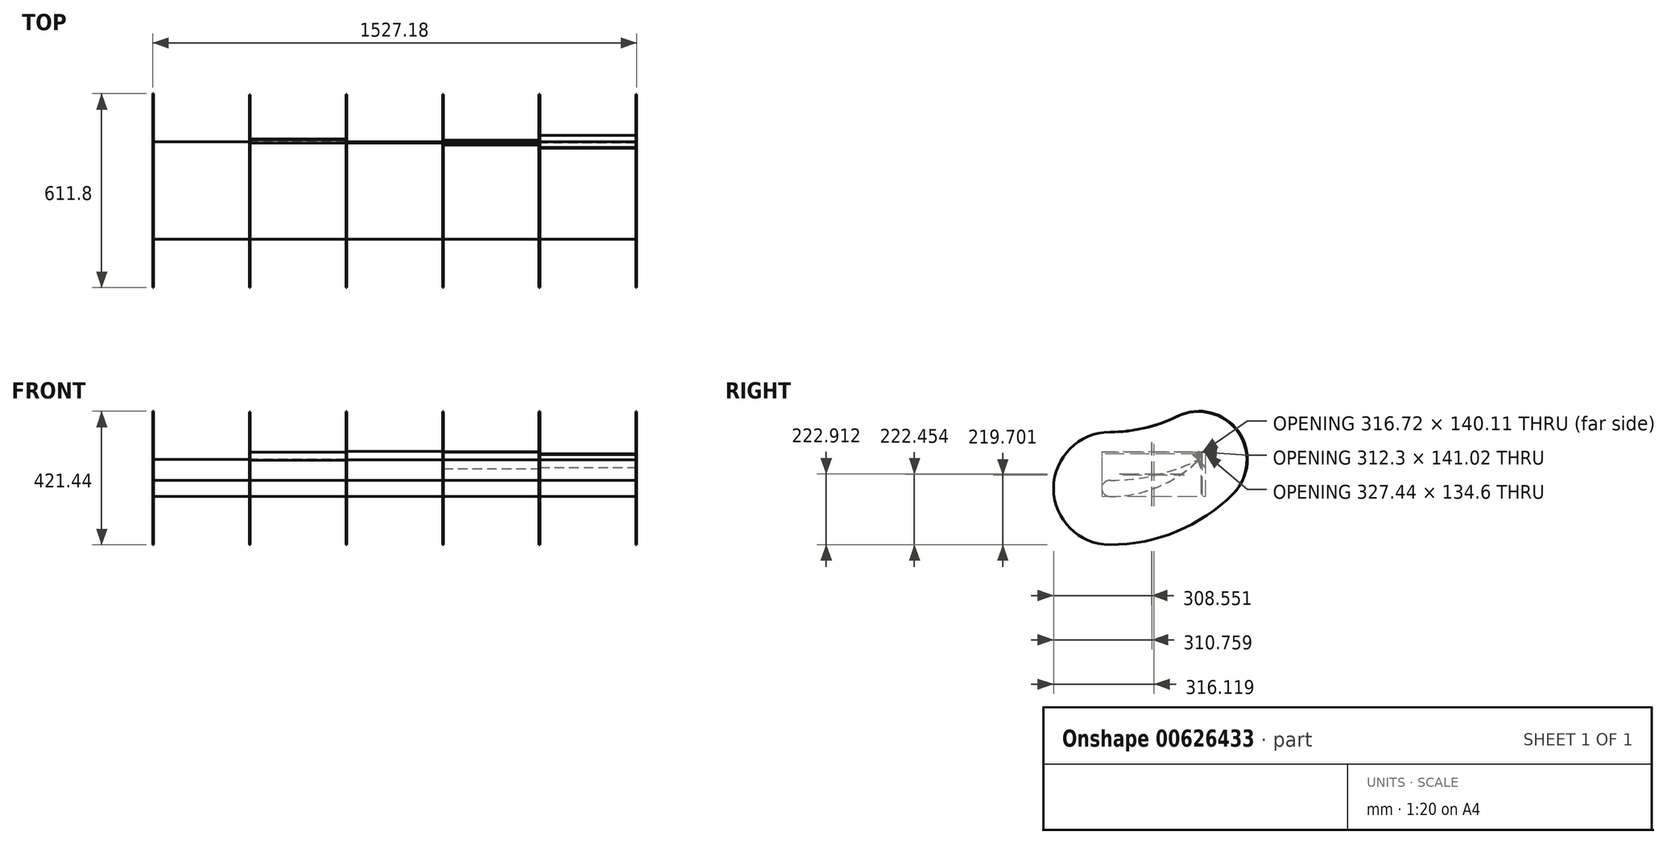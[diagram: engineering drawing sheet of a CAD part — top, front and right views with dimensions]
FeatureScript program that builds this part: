
annotation { "Feature Type Name" : "Feature", "Feature Type Description" : "" }
export const myFeature = defineFeature(function(context is Context, id is Id, definition is map)
    precondition{}
    {
        {
            var Q0;
            Q0=qCreatedBy(makeId("Right.planeOp"),FACE);
            var sketch = newSketch(context, id + "F0", { "sketchPlane" : qUnion([Q0])});
            skArc(sketch, "E0", {"start": v(0, -398.24) * mm, "mid": v(152.4, -367.93) * mm, "end": v(281.6, -281.6) * mm});
            skArc(sketch, "E1", {"start": v(0, -398.24) * mm, "mid": v(-25.4, -372.84) * mm, "end": v(0, -347.44) * mm});
            skArc(sketch, "E2", {"start": v(0, -347.44) * mm, "mid": v(144.6, -330.76) * mm, "end": v(281.6, -281.6) * mm});
            skLineSegment(sketch, "E3", {"start": v(0, 0) * mm, "end": v(281.6, -281.6) * mm});
            skSolve(sketch);
        }
        {
            var Q0;
            Q0=qSketchRegion(id+"F0",true);
            extrude(context, id + "F1", {"entities" : qUnion([Q0]), "depth" : 1524 * mm, "offsetDistance" : 25.4 * mm});
        }
        {
            var Q0;
            Q0=makeQuery(id+"F1.opExtrude","CAP_VERTEX",VERTEX,{"disambiguationData":[OSD([sQuery(id+"F0.wireOp",EDGE,"E0"),sQuery(id+"F0.wireOp",EDGE,"E1"),sQuery(id+"F0.wireOp",EDGE,"b3eccc3d-6429-4b34-9fe6-7e9520ef1e49")])],"isStart":false});
            var Q1;
            Q1=makeQuery(id+"F1.opExtrude","CAP_VERTEX",VERTEX,{"disambiguationData":[OSD([sQuery(id+"F0.wireOp",EDGE,"E1"),sQuery(id+"F0.wireOp",EDGE,"E2"),sQuery(id+"F0.wireOp",EDGE,"b3eccc3d-6429-4b34-9fe6-7e9520ef1e49")])],"isStart":false});
            var Q2;
            Q2=makeQuery(id+"F1.opExtrude","CAP_VERTEX",VERTEX,{"disambiguationData":[OSD([sQuery(id+"F0.wireOp",EDGE,"E0"),sQuery(id+"F0.wireOp",EDGE,"E2")])],"isStart":false});
            cPlane(context, id + "F2", {"entities" : qUnion([Q0, Q1, Q2]), "cplaneType" : CPlaneType.THREE_POINT, "offset" : 25.4 * mm, "width" : 152.4 * mm, "height" : 152.4 * mm});
        }
        {
            var Q0;
            Q0=qCreatedBy(id+"F2.planeOp",FACE);
            var sketch = newSketch(context, id + "F3", { "sketchPlane" : qUnion([Q0])});
            skLineSegment(sketch, "E4", {"start": v(281.6, -281.6) * mm, "end": v(263.64, -263.64) * mm});
            skLineSegment(sketch, "E5", {"start": v(263.64, -263.64) * mm, "end": v(261.4, -265.88) * mm});
            skLineSegment(sketch, "E6", {"start": v(261.4, -265.88) * mm, "end": v(302.04, -306.53) * mm});
            skLineSegment(sketch, "E7", {"start": v(281.6, -281.6) * mm, "end": v(302.04, -306.53) * mm});
            skSolve(sketch);
        }
        {
            var Q0;
            Q0=makeQuery(id+"F3.imprint","IMPRINT",FACE,{"disambiguationData":[TD([[makeQuery(id+"F3.imprint","IMPRINT",EDGE,{"derivedFrom":sQuery(id+"F3.wireOp",EDGE,"E4")}),1.0]])]});
            extrude(context, id + "F4", {"entities" : qUnion([Q0]), "operationType" : NewBodyOperationType.ADD, "oppositeDirection" : true, "depth" : 304.8 * mm, "offsetDistance" : 25.4 * mm});
        }
        {
            var Q0;
            Q0=qCreatedBy(id+"F2.planeOp",FACE);
            cPlane(context, id + "F5", {"entities" : qUnion([Q0]), "cplaneType" : CPlaneType.OFFSET, "offset" : 304.8 * mm, "oppositeDirection" : true, "width" : 152.4 * mm, "height" : 152.4 * mm});
        }
        {
            var Q0;
            Q0=qCreatedBy(id+"F5.planeOp",FACE);
            var sketch = newSketch(context, id + "F6", { "sketchPlane" : qUnion([Q0])});
            skPoint(sketch, "E8.0", {"position": v(281.6, -281.6) * mm});
            skLineSegment(sketch, "E9", {"start": v(281.6, -281.6) * mm, "end": v(274.48, -257.22) * mm});
            skLineSegment(sketch, "E10", {"start": v(274.48, -257.22) * mm, "end": v(271.43, -258.1) * mm});
            skLineSegment(sketch, "E11", {"start": v(271.43, -258.1) * mm, "end": v(286.9, -311.1) * mm});
            skLineSegment(sketch, "E12", {"start": v(286.9, -311.1) * mm, "end": v(281.6, -281.6) * mm});
            skSolve(sketch);
        }
        {
            var Q0;
            Q0=qSketchRegion(id+"F6",true);
            extrude(context, id + "F7", {"entities" : qUnion([Q0]), "operationType" : NewBodyOperationType.ADD, "oppositeDirection" : true, "depth" : 304.8 * mm, "offsetDistance" : 25.4 * mm});
        }
        {
            var Q0;
            Q0=qCreatedBy(id+"F5.planeOp",FACE);
            cPlane(context, id + "F8", {"entities" : qUnion([Q0]), "cplaneType" : CPlaneType.OFFSET, "offset" : 304.8 * mm, "oppositeDirection" : true, "width" : 152.4 * mm, "height" : 152.4 * mm});
        }
        {
            var Q0;
            Q0=qCreatedBy(id+"F8.planeOp",FACE);
            var sketch = newSketch(context, id + "F9", { "sketchPlane" : qUnion([Q0])});
            skPoint(sketch, "E13.0", {"position": v(281.6, -281.6) * mm});
            skLineSegment(sketch, "E14", {"start": v(281.6, -281.6) * mm, "end": v(281.6, -256.2) * mm});
            skLineSegment(sketch, "E15", {"start": v(281.6, -256.2) * mm, "end": v(278.42, -256.2) * mm});
            skLineSegment(sketch, "E16", {"start": v(278.42, -256.2) * mm, "end": v(278.42, -284.14) * mm});
            skLineSegment(sketch, "E17", {"start": v(278.42, -284.14) * mm, "end": v(281.6, -281.6) * mm});
            skSolve(sketch);
        }
        {
            var Q0;
            Q0=qSketchRegion(id+"F9",true);
            extrude(context, id + "F10", {"entities" : qUnion([Q0]), "operationType" : NewBodyOperationType.ADD, "oppositeDirection" : true, "depth" : 304.8 * mm, "offsetDistance" : 25.4 * mm});
        }
        {
            var Q0;
            Q0=qCreatedBy(id+"F8.planeOp",FACE);
            cPlane(context, id + "F11", {"entities" : qUnion([Q0]), "cplaneType" : CPlaneType.OFFSET, "offset" : 304.8 * mm, "oppositeDirection" : true, "width" : 152.4 * mm, "height" : 152.4 * mm});
        }
        {
            var Q0;
            Q0=qCreatedBy(id+"F11.planeOp",FACE);
            cPlane(context, id + "F12", {"entities" : qUnion([Q0]), "cplaneType" : CPlaneType.OFFSET, "offset" : 304.8 * mm, "oppositeDirection" : true, "width" : 152.4 * mm, "height" : 152.4 * mm});
        }
        {
            var Q0;
            Q0=makeQuery(id+"F1.opExtrude","CAP_FACE",FACE,{"disambiguationData":[OSD([sQuery(id+"F0.wireOp",EDGE,"E0"),sQuery(id+"F0.wireOp",EDGE,"E1"),sQuery(id+"F0.wireOp",EDGE,"E2")])],"isStart":true});
            var sketch = newSketch(context, id + "F13", { "sketchPlane" : qUnion([Q0])});
            skArc(sketch, "E18.0", {"start": v(0, -195.04) * mm, "mid": v(-109.9, -182.36) * mm, "end": v(-214.03, -145) * mm});
            skArc(sketch, "E19.0", {"start": v(0, -550.64) * mm, "mid": v(177.8, -372.84) * mm, "end": v(0, -195.04) * mm});
            skArc(sketch, "E20.0", {"start": v(0, -550.64) * mm, "mid": v(-210.72, -508.73) * mm, "end": v(-389.36, -389.36) * mm});
            skArc(sketch, "E21", {"start": v(-214.03, -145) * mm, "mid": v(-405.42, -192.75) * mm, "end": v(-389.36, -389.36) * mm});
            skSolve(sketch);
        }
        {
            var Q0;
            Q0=qSketchRegion(id+"F13",true);
            extrude(context, id + "F14", {"entities" : qUnion([Q0]), "operationType" : NewBodyOperationType.ADD, "endBound" : BoundingType.SYMMETRIC, "depth" : 3.17 * mm, "offsetDistance" : 25.4 * mm});
        }
        {
            var Q0;
            Q0=qCreatedBy(id+"F11.planeOp",FACE);
            var sketch = newSketch(context, id + "F15", { "sketchPlane" : qUnion([Q0])});
            skArc(sketch, "E22.0", {"start": v(0, -195.04) * mm, "mid": v(108.76, -182.63) * mm, "end": v(211.93, -146.03) * mm});
            skArc(sketch, "E23.0", {"start": v(0, -550.64) * mm, "mid": v(210.72, -508.73) * mm, "end": v(389.36, -389.36) * mm});
            skArc(sketch, "E24", {"start": v(0, -195.04) * mm, "mid": v(-177.8, -372.84) * mm, "end": v(0, -550.64) * mm});
            skArc(sketch, "E25", {"start": v(211.93, -146.03) * mm, "mid": v(402.63, -193.33) * mm, "end": v(389.36, -389.36) * mm});
            skSolve(sketch);
        }
        {
            var Q0;
            Q0=qSketchRegion(id+"F15",true);
            extrude(context, id + "F16", {"entities" : qUnion([Q0]), "operationType" : NewBodyOperationType.ADD, "endBound" : BoundingType.SYMMETRIC, "depth" : 3.17 * mm, "offsetDistance" : 25.4 * mm});
        }
        {
            var Q0;
            Q0=qCreatedBy(id+"F8.planeOp",FACE);
            var sketch = newSketch(context, id + "F17", { "sketchPlane" : qUnion([Q0])});
            skArc(sketch, "E26.0", {"start": v(0, -195.04) * mm, "mid": v(108.76, -182.63) * mm, "end": v(211.93, -146.03) * mm});
            skArc(sketch, "E27.0", {"start": v(0, -550.64) * mm, "mid": v(210.72, -508.73) * mm, "end": v(389.36, -389.36) * mm});
            skArc(sketch, "E28", {"start": v(0, -195.04) * mm, "mid": v(-177.8, -372.84) * mm, "end": v(0, -550.64) * mm});
            skArc(sketch, "E29", {"start": v(211.93, -146.03) * mm, "mid": v(402.63, -193.33) * mm, "end": v(389.36, -389.36) * mm});
            skSolve(sketch);
        }
        {
            var Q0;
            Q0=qSketchRegion(id+"F17",true);
            extrude(context, id + "F18", {"entities" : qUnion([Q0]), "operationType" : NewBodyOperationType.ADD, "endBound" : BoundingType.SYMMETRIC, "depth" : 3.17 * mm, "offsetDistance" : 25.4 * mm});
        }
        {
            var Q0;
            Q0=qCreatedBy(id+"F5.planeOp",FACE);
            var sketch = newSketch(context, id + "F19", { "sketchPlane" : qUnion([Q0])});
            skArc(sketch, "E30.0", {"start": v(0, -195.04) * mm, "mid": v(108.76, -182.63) * mm, "end": v(211.93, -146.03) * mm});
            skArc(sketch, "E31.0", {"start": v(0, -550.64) * mm, "mid": v(210.72, -508.73) * mm, "end": v(389.36, -389.36) * mm});
            skArc(sketch, "E32", {"start": v(0, -195.04) * mm, "mid": v(-177.8, -372.84) * mm, "end": v(0, -550.64) * mm});
            skArc(sketch, "E33", {"start": v(211.93, -146.03) * mm, "mid": v(402.63, -193.33) * mm, "end": v(389.36, -389.36) * mm});
            skSolve(sketch);
        }
        {
            var Q0;
            Q0=qSketchRegion(id+"F19",true);
            extrude(context, id + "F20", {"entities" : qUnion([Q0]), "operationType" : NewBodyOperationType.ADD, "endBound" : BoundingType.SYMMETRIC, "depth" : 3.17 * mm, "offsetDistance" : 25.4 * mm});
        }
        {
            var Q0;
            Q0=qCreatedBy(id+"F2.planeOp",FACE);
            var sketch = newSketch(context, id + "F21", { "sketchPlane" : qUnion([Q0])});
            skArc(sketch, "E34.0", {"start": v(0, -195.04) * mm, "mid": v(108.76, -182.63) * mm, "end": v(211.93, -146.03) * mm});
            skArc(sketch, "E35.0", {"start": v(0, -550.64) * mm, "mid": v(210.72, -508.73) * mm, "end": v(389.36, -389.36) * mm});
            skArc(sketch, "E36", {"start": v(0, -195.04) * mm, "mid": v(-177.8, -372.84) * mm, "end": v(0, -550.64) * mm});
            skArc(sketch, "E37", {"start": v(211.93, -146.03) * mm, "mid": v(402.63, -193.33) * mm, "end": v(389.36, -389.36) * mm});
            skSolve(sketch);
        }
        {
            var Q0;
            Q0=qSketchRegion(id+"F21",true);
            extrude(context, id + "F22", {"entities" : qUnion([Q0]), "operationType" : NewBodyOperationType.ADD, "endBound" : BoundingType.SYMMETRIC, "depth" : 3.17 * mm, "offsetDistance" : 25.4 * mm});
        }
        {
            var Q0;
            Q0=qCreatedBy(id+"F11.planeOp",FACE);
            var sketch = newSketch(context, id + "F23", { "sketchPlane" : qUnion([Q0])});
            skPoint(sketch, "E38.0", {"position": v(281.6, -281.6) * mm});
            skLineSegment(sketch, "E39", {"start": v(281.6, -281.6) * mm, "end": v(291.32, -258.13) * mm});
            skLineSegment(sketch, "E40", {"start": v(291.32, -258.13) * mm, "end": v(288.14, -258.13) * mm});
            skLineSegment(sketch, "E41", {"start": v(288.14, -258.13) * mm, "end": v(277.45, -283.95) * mm});
            skLineSegment(sketch, "E42", {"start": v(277.45, -283.95) * mm, "end": v(281.6, -281.6) * mm});
            skSolve(sketch);
        }
        {
            var Q0;
            Q0=qSketchRegion(id+"F23",true);
            extrude(context, id + "F24", {"entities" : qUnion([Q0]), "operationType" : NewBodyOperationType.ADD, "oppositeDirection" : true, "depth" : 304.8 * mm, "offsetDistance" : 25.4 * mm});
        }
        {
            var Q0;
            Q0=qCreatedBy(id+"F12.planeOp",FACE);
            var sketch = newSketch(context, id + "F25", { "sketchPlane" : qUnion([Q0])});
            skArc(sketch, "E43.0", {"start": v(0, -195.04) * mm, "mid": v(108.33, -182.73) * mm, "end": v(211.13, -146.42) * mm});
            skArc(sketch, "E44.0", {"start": v(0, -550.64) * mm, "mid": v(210.72, -508.73) * mm, "end": v(389.36, -389.36) * mm});
            skArc(sketch, "E45", {"start": v(0, -195.04) * mm, "mid": v(-177.8, -372.84) * mm, "end": v(0, -550.64) * mm});
            skArc(sketch, "E46", {"start": v(211.13, -146.42) * mm, "mid": v(401.59, -193.55) * mm, "end": v(389.36, -389.36) * mm});
            skSolve(sketch);
        }
        {
            var Q0;
            Q0=qSketchRegion(id+"F25",true);
            extrude(context, id + "F26", {"entities" : qUnion([Q0]), "operationType" : NewBodyOperationType.ADD, "endBound" : BoundingType.SYMMETRIC, "depth" : 3.17 * mm, "offsetDistance" : 25.4 * mm});
        }
    });
